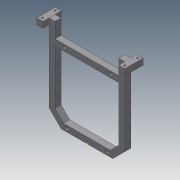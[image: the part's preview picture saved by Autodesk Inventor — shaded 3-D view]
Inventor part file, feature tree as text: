
AUTODESK INVENTOR PART (.ipt)
format: ipt  version: 2014 SP1 (Build 180222100, 222)  size: 154,624 bytes
history: native  units: in
note: dims shown in document units (in); Inventor stores cm internally (conversion verified against a paired STEP export)
features: extrude x3, mirror x2, sketch x2
ambient origin geometry x8: Origin, YZ Plane, XZ Plane, XY Plane, X Axis, Y Axis, Z Axis, Center Point
bodies: Solid1 (feature_tree)
feature tree (7):
  extrude  "Extrusion1"  Depth=5.67in
  extrude  "Extrusion4"  Depth=0.5in
  mirror  "Mirror1"
  extrude  "Extrusion5"  Depth=0.5in
  mirror  "Mirror2"
  sketch  "Sketch4"  dims[d1=5.67in d2=0.25in]
  sketch  "Sketch6"  dims[d3=0.25in d4=0.5in d5=0.5in d8=0.5in d9=0.0in d15=0.5in d16=0.5in d17=0.5in d18=0.0in d20=1.0in d21=0.0in d22=0.25in d23=0.25in d24=0.25in d25=0.25in d26=0.25in d27=0.25in d28=0.5in d29=0.0in d30=0.5305in d31=1.061in]
